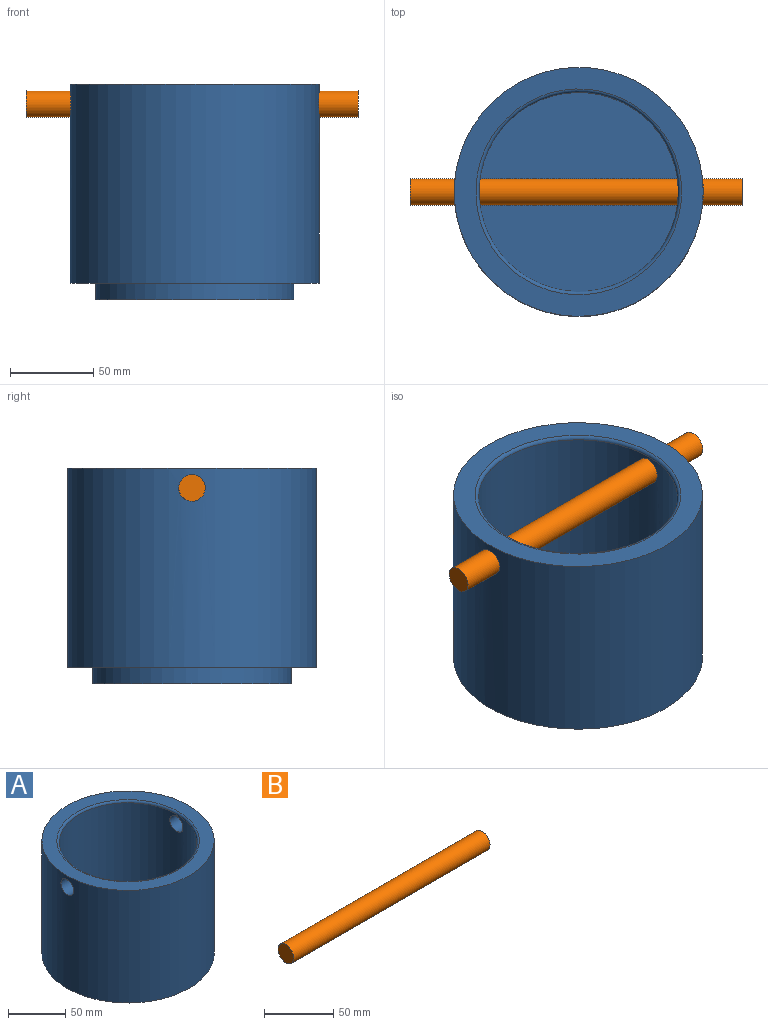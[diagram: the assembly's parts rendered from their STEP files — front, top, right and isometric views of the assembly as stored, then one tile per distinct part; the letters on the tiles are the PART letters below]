
ASSEMBLY  parts=2 mates=2
PART A: 10 faces, bbox 150x150x130 mm
  f0: cylinder r=75mm len=150mm, axis (0,0,-1), area 56145.9mm2, adj f2,f5,f7,f8
  f1: cylinder r=60mm len=120mm, axis (0,0,1), area 32771.4mm2, adj f3,f7,f8,f9
  f2: plane 150x150mm, normal (0,0,1), area 5595.2mm2, adj f0,f9
  f3: plane 120x120mm, normal (0,0,1), area 11309.7mm2, adj f1
  f4: cylinder r=59.75mm len=119.5mm, axis (0,0,-1), area 3754.2mm2, adj f5,f6
  f5: plane 150x150mm, normal (0,0,-1), area 6455.8mm2, adj f0,f4
  f6: plane 119.5x119.5mm, normal (0,0,-1), area 11215.7mm2, adj f4
  f7: cylinder r=8mm len=16mm, axis (1,0,0), area 756.7mm2, adj f0,f1
  f8: cylinder r=8mm len=16mm, axis (-1,0,0), area 756.7mm2, adj f0,f1
  f9: torus R=62mm, axis (0,0,1), area 1198.7mm2, adj f1,f2
PART B: 3 faces, bbox 200x16x16 mm
  f0: cylinder r=8mm len=200mm, axis (-1,0,0), area 10053.1mm2, adj f1,f2
  f1: plane 16x16mm, normal (1,0,0), area 201.1mm2, adj f0
  f2: plane 16x16mm, normal (-1,0,0), area 201.1mm2, adj f0
PLACE A t=(30.64,-11.88,61.9)mm
PLACE B t=(-71.02,-11.88,179.9)mm fixed
MATE cylindrical B.f0 <-> A.f7  axis (-1,0,0) through (28.98,-11.88,179.9)mm
MATE parallel B.f0 <-> A.f7  axis (-1,0,0) through (128.98,-11.88,179.9)mm
